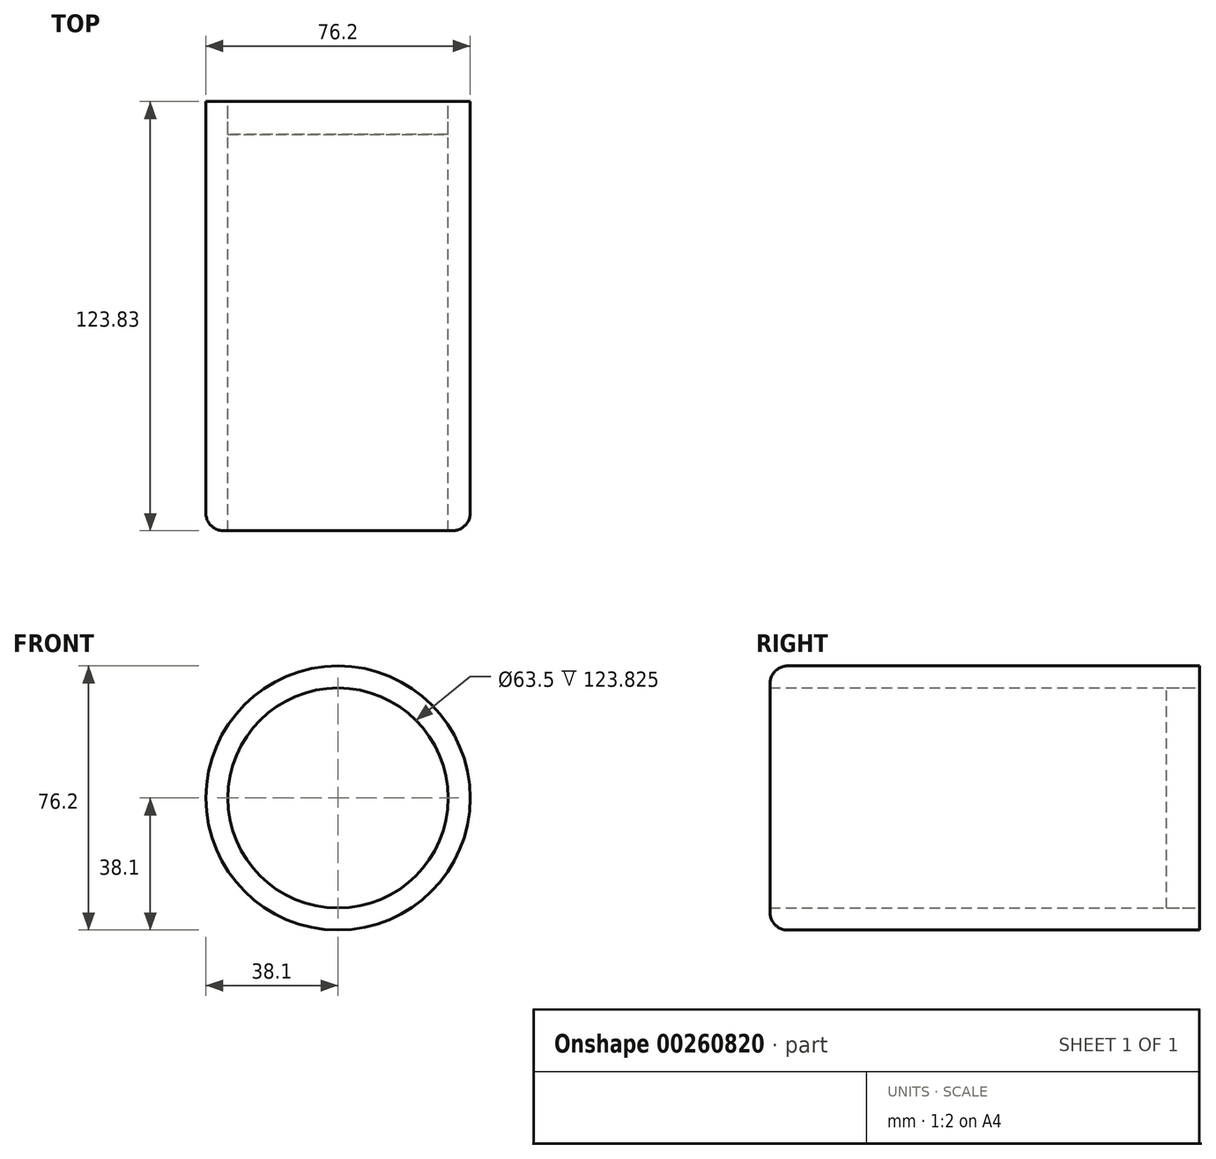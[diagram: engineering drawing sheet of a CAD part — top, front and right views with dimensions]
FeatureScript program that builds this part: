
annotation { "Feature Type Name" : "Feature", "Feature Type Description" : "" }
export const myFeature = defineFeature(function(context is Context, id is Id, definition is map)
    precondition{}
    {
        {
            var Q0;
            Q0=qCreatedBy(makeId("Front.planeOp"),FACE);
            var sketch = newSketch(context, id + "F0", { "sketchPlane" : qUnion([Q0])});
            skCircle(sketch, "E0", {"center": v(0, 0) * mm, "radius": 38.1 * mm});
            skCircle(sketch, "E1", {"center": v(0, 0) * mm, "radius": 31.75 * mm});
            skSolve(sketch);
        }
        {
            var Q0;
            Q0=makeQuery(id+"F0.imprint","IMPRINT",FACE,{"disambiguationData":[TD([[makeQuery(id+"F0.imprint","IMPRINT",EDGE,{"derivedFrom":sQuery(id+"F0.wireOp",EDGE,"E1")}),1.0]])]});
            extrude(context, id + "F1", {"entities" : qUnion([Q0]), "depth" : 9.52 * mm});
        }
        {
            var Q0;
            Q0=makeQuery(id+"F0.imprint","IMPRINT",FACE,{"disambiguationData":[TD([[makeQuery(id+"F0.imprint","IMPRINT",EDGE,{"derivedFrom":sQuery(id+"F0.wireOp",EDGE,"E0")}),1.0]])]});
            extrude(context, id + "F2", {"entities" : qUnion([Q0]), "depth" : 123.82 * mm});
        }
        {
            var Q0;
            Q0=makeQuery(id+"F2.opExtrude","CAP_EDGE",EDGE,{"disambiguationData":[OSD([sQuery(id+"F0.wireOp",EDGE,"E0")])],"isStart":false});
            fillet(context, id + "F3", {"entities" : qUnion([Q0]), "radius" : 5.08 * mm, "tangentPropagation" : true, "allowEdgeOverflow" : false});
        }
    });
